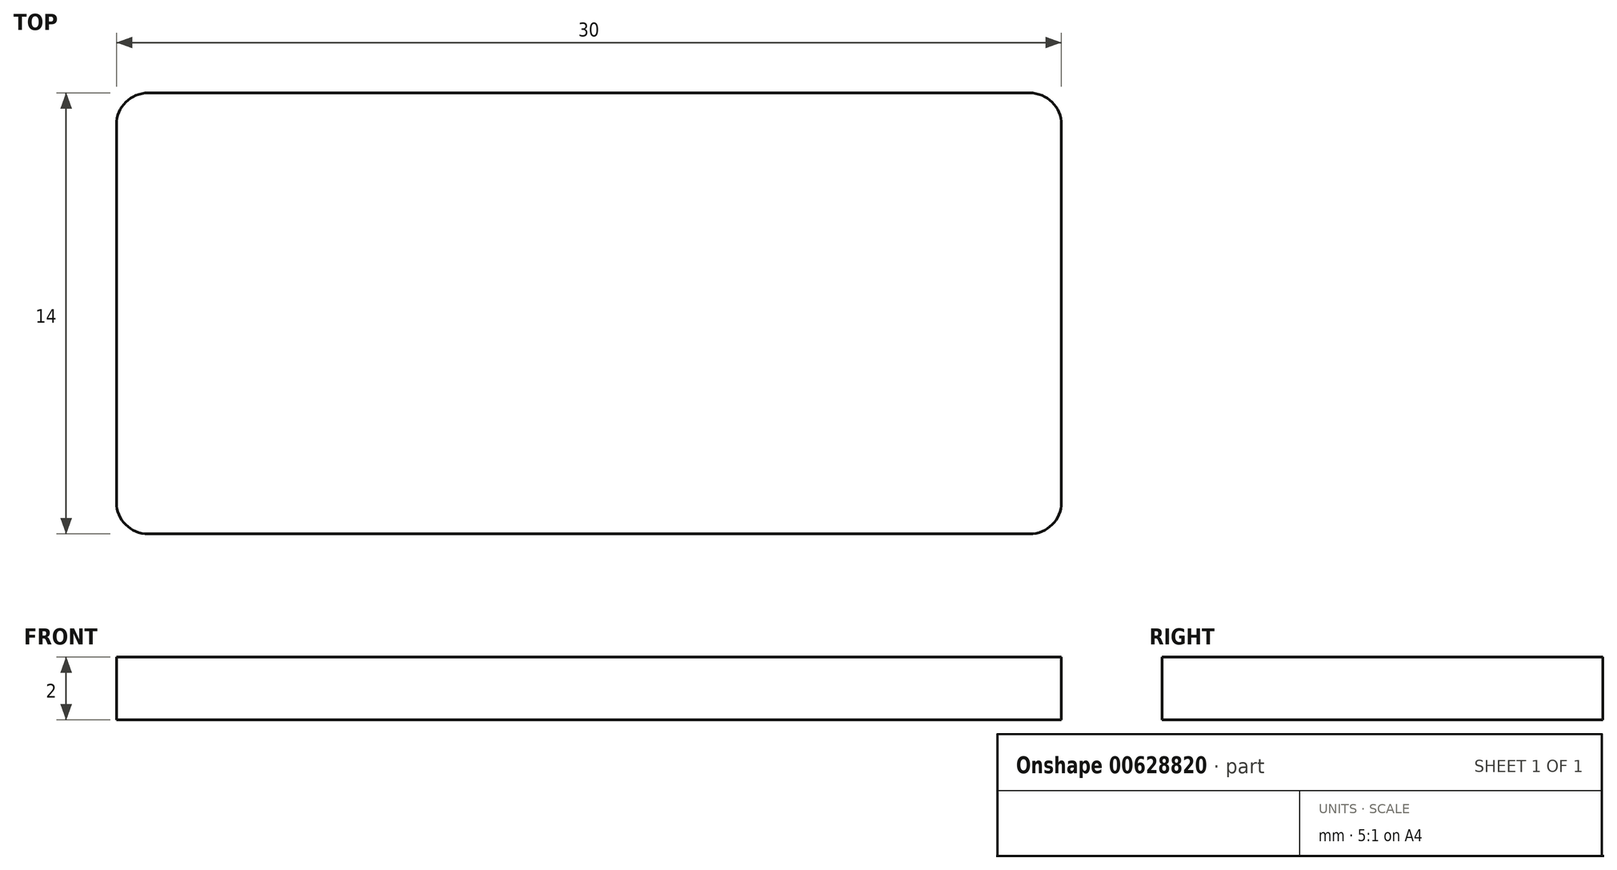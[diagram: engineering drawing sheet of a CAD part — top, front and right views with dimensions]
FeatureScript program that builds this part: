
annotation { "Feature Type Name" : "Feature", "Feature Type Description" : "" }
export const myFeature = defineFeature(function(context is Context, id is Id, definition is map)
    precondition{}
    {
        {
            var Q0;
            Q0=qCreatedBy(makeId("Top.planeOp"),FACE);
            var sketch = newSketch(context, id + "F0", { "sketchPlane" : qUnion([Q0])});
            skLineSegment(sketch, "E0.bottom", {"start": v(14, 7) * mm, "end": v(-14, 7) * mm});
            skLineSegment(sketch, "E0.top", {"start": v(14, -7) * mm, "end": v(-14, -7) * mm});
            skLineSegment(sketch, "E0.left", {"start": v(15, 6) * mm, "end": v(15, -6) * mm});
            skLineSegment(sketch, "E0.right", {"start": v(-15, 6) * mm, "end": v(-15, -6) * mm});
            skPoint(sketch, "E0.middle", {"position": v(0, 0) * mm});
            skPoint(sketch, "E1.visualSharp", {"position": v(-15, 7) * mm});
            skArc(sketch, "E1.filletArc", {"start": v(-14, 7) * mm, "mid": v(-14.7, 6.7) * mm, "end": v(-15, 6) * mm});
            skPoint(sketch, "E2.visualSharp", {"position": v(15, 7) * mm});
            skArc(sketch, "E2.filletArc", {"start": v(15, 6) * mm, "mid": v(14.7, 6.7) * mm, "end": v(14, 7) * mm});
            skPoint(sketch, "E3.visualSharp", {"position": v(15, -7) * mm});
            skArc(sketch, "E3.filletArc", {"start": v(14, -7) * mm, "mid": v(14.7, -6.7) * mm, "end": v(15, -6) * mm});
            skPoint(sketch, "E4.visualSharp", {"position": v(-15, -7) * mm});
            skArc(sketch, "E4.filletArc", {"start": v(-15, -6) * mm, "mid": v(-14.7, -6.7) * mm, "end": v(-14, -7) * mm});
            skSolve(sketch);
        }
        {
            var Q0;
            Q0 = qSketchRegion(id + "F0", true);
            extrude(context, id + "F1", {"entities" : qUnion([Q0]), "oppositeDirection" : true, "depth" : 2 * mm, "offsetDistance" : 25 * mm, "symmetric" : true});
        }
    });
